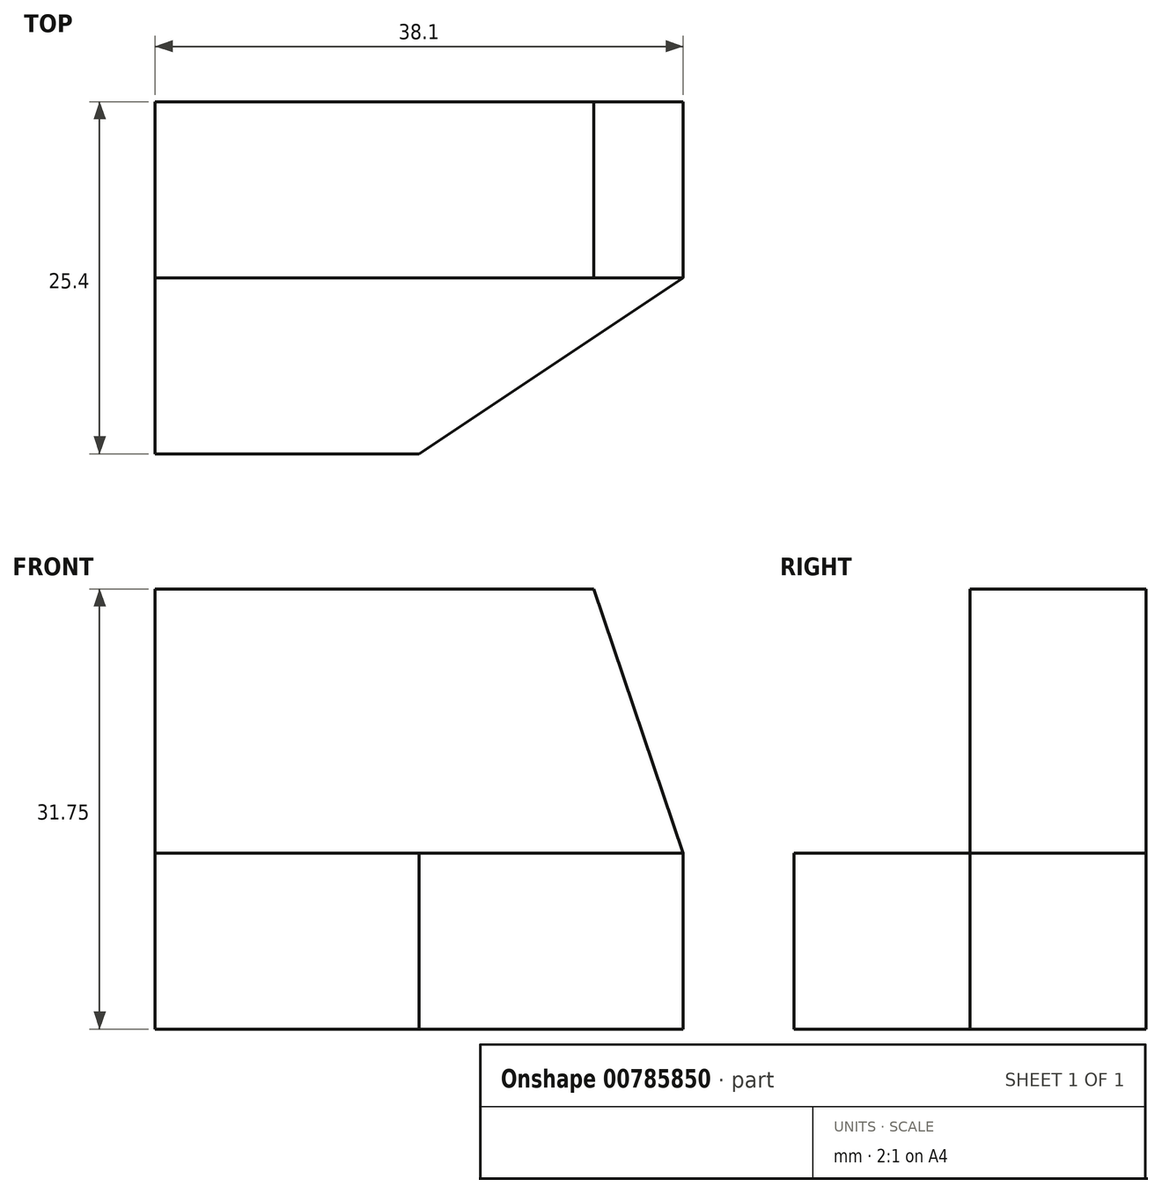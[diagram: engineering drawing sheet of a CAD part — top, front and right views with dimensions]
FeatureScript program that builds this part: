
annotation { "Feature Type Name" : "Feature", "Feature Type Description" : "" }
export const myFeature = defineFeature(function(context is Context, id is Id, definition is map)
    precondition{}
    {
        {
            var Q0;
            Q0=qCreatedBy(makeId("Right.planeOp"),FACE);
            var sketch = newSketch(context, id + "F0", { "sketchPlane" : qUnion([Q0])});
            skLineSegment(sketch, "E0", {"start": v(0, 0) * mm, "end": v(12.7, 0) * mm});
            skLineSegment(sketch, "E1", {"start": v(12.7, 0) * mm, "end": v(12.7, 19.05) * mm});
            skLineSegment(sketch, "E2", {"start": v(12.7, 19.05) * mm, "end": v(25.4, 19.05) * mm});
            skLineSegment(sketch, "E3", {"start": v(25.4, 19.05) * mm, "end": v(25.4, 0) * mm});
            skLineSegment(sketch, "E4", {"start": v(12.7, 0) * mm, "end": v(25.4, 0) * mm});
            skLineSegment(sketch, "E5", {"start": v(0, 0) * mm, "end": v(0, -12.7) * mm});
            skLineSegment(sketch, "E6", {"start": v(12.7, 0) * mm, "end": v(12.7, -12.7) * mm});
            skLineSegment(sketch, "E7", {"start": v(0, -12.7) * mm, "end": v(12.7, -12.7) * mm});
            skLineSegment(sketch, "E8", {"start": v(12.7, -12.7) * mm, "end": v(25.4, -12.7) * mm});
            skLineSegment(sketch, "E9", {"start": v(25.4, 0) * mm, "end": v(25.4, -12.7) * mm});
            skSolve(sketch);
        }
        {
            var Q0;
            Q0 = qSketchRegion(id + "F0", true);
            extrude(context, id + "F1", {"entities" : qUnion([Q0]), "depth" : 38.1 * mm, "offsetDistance" : 25.4 * mm});
        }
        {
            var Q0;
            Q0=makeQuery(id+"F1.opExtrude","CAP_FACE",FACE,{"disambiguationData":[OSD([sQuery(id+"F0.wireOp",EDGE,"E0"),sQuery(id+"F0.wireOp",EDGE,"E1"),sQuery(id+"F0.wireOp",EDGE,"E2"),sQuery(id+"F0.wireOp",EDGE,"E3"),sQuery(id+"F0.wireOp",EDGE,"E5"),sQuery(id+"F0.wireOp",EDGE,"E7"),sQuery(id+"F0.wireOp",EDGE,"E8"),sQuery(id+"F0.wireOp",EDGE,"E9")])],"isStart":false});
            var sketch = newSketch(context, id + "F2", { "sketchPlane" : qUnion([Q0])});
            skLineSegment(sketch, "E10", {"start": v(12.7, 0) * mm, "end": v(25.4, 0) * mm});
            skSolve(sketch);
        }
        {
            var Q0;
            Q0=makeQuery(id+"F1.opExtrude","SWEPT_FACE",FACE,{"disambiguationData":[OSD([sQuery(id+"F0.wireOp",EDGE,"E1")])]});
            var sketch = newSketch(context, id + "F3", { "sketchPlane" : qUnion([Q0])});
            skLineSegment(sketch, "E11", {"start": v(31.64, 19.05) * mm, "end": v(38.1, 0) * mm});
            skSolve(sketch);
        }
        {
            var Q0;
            {var subQ0=sQuery(id+"F3.wireOp",EDGE,"E11");Q0=makeQuery(id+"F3.imprint","IMPRINT",FACE,{"disambiguationData":[TD([[makeQuery(id+"F3.imprint","IMPRINT",EDGE,{"derivedFrom":subQ0}),1.0]])]});}
            extrude(context, id + "F4", {"entities" : qUnion([Q0]), "operationType" : NewBodyOperationType.REMOVE, "oppositeDirection" : true, "depth" : 25.4 * mm, "offsetDistance" : 25.4 * mm});
        }
        {
            var Q0;
            Q0=makeQuery(id+"F1.opExtrude","SWEPT_FACE",FACE,{"disambiguationData":[OSD([sQuery(id+"F0.wireOp",EDGE,"E0")])]});
            var sketch = newSketch(context, id + "F5", { "sketchPlane" : qUnion([Q0])});
            skLineSegment(sketch, "E12", {"start": v(0, 0) * mm, "end": v(19.05, 0) * mm});
            skLineSegment(sketch, "E13", {"start": v(19.05, 0) * mm, "end": v(38.1, 12.7) * mm});
            skSolve(sketch);
        }
        {
            var Q0;
            {var subQ0=sQuery(id+"F5.wireOp",EDGE,"E13");Q0=makeQuery(id+"F5.imprint","IMPRINT",FACE,{"disambiguationData":[TD([[makeQuery(id+"F5.imprint","IMPRINT",EDGE,{"derivedFrom":subQ0}),-1.0]])]});}
            extrude(context, id + "F6", {"entities" : qUnion([Q0]), "operationType" : NewBodyOperationType.REMOVE, "oppositeDirection" : true, "depth" : 25.4 * mm, "offsetDistance" : 25.4 * mm});
        }
    });
